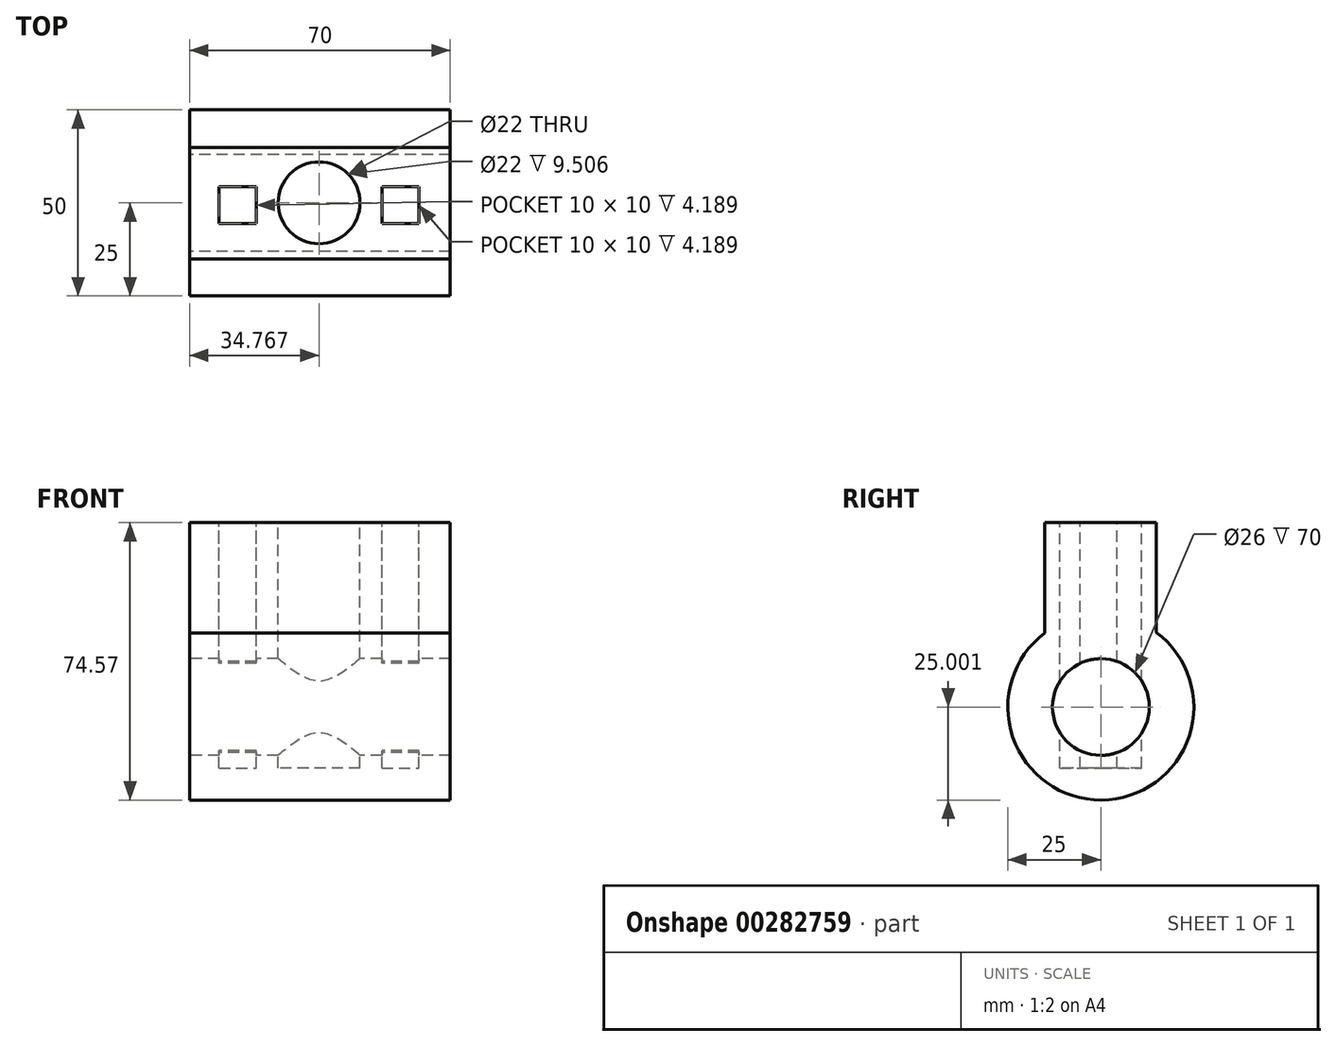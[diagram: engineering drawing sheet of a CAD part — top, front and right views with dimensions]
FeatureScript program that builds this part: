
annotation { "Feature Type Name" : "Feature", "Feature Type Description" : "" }
export const myFeature = defineFeature(function(context is Context, id is Id, definition is map)
    precondition{}
    {
        {
            var Q0;
            Q0=qCreatedBy(makeId("Top.planeOp"),FACE);
            var sketch = newSketch(context, id + "F0", { "sketchPlane" : qUnion([Q0])});
            skLineSegment(sketch, "E0.bottom", {"start": v(-48.83, 13.42) * mm, "end": v(21.17, 13.42) * mm});
            skLineSegment(sketch, "E0.top", {"start": v(-48.83, -16.58) * mm, "end": v(21.17, -16.58) * mm});
            skLineSegment(sketch, "E0.left", {"start": v(-48.83, 13.42) * mm, "end": v(-48.83, -16.58) * mm});
            skLineSegment(sketch, "E0.right", {"start": v(21.17, 13.42) * mm, "end": v(21.17, -16.58) * mm});
            skSolve(sketch);
        }
        {
            var Q0;
            Q0=makeQuery(id+"F0.imprint","IMPRINT",FACE,{"disambiguationData":[TD([[makeQuery(id+"F0.imprint","IMPRINT",EDGE,{"derivedFrom":sQuery(id+"F0.wireOp",EDGE,"E0.bottom")}),-1.0]])]});
            extrude(context, id + "F1", {"entities" : qUnion([Q0]), "depth" : 66 * mm});
        }
        {
            var Q0;
            Q0=makeQuery(id+"F1.opExtrude","CAP_FACE",FACE,{"disambiguationData":[OSD([sQuery(id+"F0.wireOp",EDGE,"E0.bottom"),sQuery(id+"F0.wireOp",EDGE,"E0.top"),sQuery(id+"F0.wireOp",EDGE,"E0.left"),sQuery(id+"F0.wireOp",EDGE,"E0.right")])],"isStart":false});
            var sketch = newSketch(context, id + "F2", { "sketchPlane" : qUnion([Q0])});
            skCircle(sketch, "E1", {"center": v(-14.06, -1.48) * mm, "radius": 11 * mm});
            skLineSegment(sketch, "E2.bottom", {"start": v(-40.94, 2.9) * mm, "end": v(-30.94, 2.9) * mm});
            skLineSegment(sketch, "E2.top", {"start": v(-40.94, -7.1) * mm, "end": v(-30.94, -7.1) * mm});
            skLineSegment(sketch, "E2.left", {"start": v(-40.94, 2.9) * mm, "end": v(-40.94, -7.1) * mm});
            skLineSegment(sketch, "E2.right", {"start": v(-30.94, 2.9) * mm, "end": v(-30.94, -7.1) * mm});
            skLineSegment(sketch, "E3.bottom", {"start": v(2.81, 2.9) * mm, "end": v(12.81, 2.9) * mm});
            skLineSegment(sketch, "E3.top", {"start": v(2.81, -7.1) * mm, "end": v(12.81, -7.1) * mm});
            skLineSegment(sketch, "E3.left", {"start": v(2.81, 2.9) * mm, "end": v(2.81, -7.1) * mm});
            skLineSegment(sketch, "E3.right", {"start": v(12.81, 2.9) * mm, "end": v(12.81, -7.1) * mm});
            skSolve(sketch);
        }
        {
            var Q0;
            Q0=makeQuery(id+"F2.imprint","IMPRINT",FACE,{"disambiguationData":[TD([[makeQuery(id+"F2.imprint","IMPRINT",EDGE,{"derivedFrom":sQuery(id+"F2.wireOp",EDGE,"E2.bottom")}),-1.0]])]});
            var Q1;
            Q1=makeQuery(id+"F2.imprint","IMPRINT",FACE,{"disambiguationData":[TD([[makeQuery(id+"F2.imprint","IMPRINT",EDGE,{"derivedFrom":sQuery(id+"F2.wireOp",EDGE,"E3.bottom")}),-1.0]])]});
            var Q2;
            Q2=makeQuery(id+"F2.imprint","IMPRINT",FACE,{"disambiguationData":[TD([[makeQuery(id+"F2.imprint","IMPRINT",EDGE,{"derivedFrom":sQuery(id+"F2.wireOp",EDGE,"E1")}),1.0]])]});
            extrude(context, id + "F3", {"entities" : qUnion([Q0, Q1, Q2]), "operationType" : NewBodyOperationType.REMOVE, "oppositeDirection" : true, "depth" : 66 * mm});
        }
        {
            var Q0;
            Q0=makeQuery(id+"F1.opExtrude","SWEPT_FACE",FACE,{"disambiguationData":[OSD([sQuery(id+"F0.wireOp",EDGE,"E0.left")])]});
            var sketch = newSketch(context, id + "F4", { "sketchPlane" : qUnion([Q0])});
            skCircle(sketch, "E4", {"center": v(1.48, 16.43) * mm, "radius": 25 * mm});
            skSolve(sketch);
        }
        {
            var Q0;
            {var subQ1=sQuery(id+"F0.wireOp",EDGE,"E0.left");var subQ6=makeQuery(id+"F1.opExtrude","CAP_EDGE",EDGE,{"disambiguationData":[OSD([subQ1])],"isStart":true});Q0=makeQuery(id+"F4.imprint","IMPRINT",FACE,{"disambiguationData":[TD([[makeQuery(id+"F4.imprint","IMPRINT",EDGE,{"derivedFrom":subQ6}),-1.0]])]});}
            extrude(context, id + "F5", {"entities" : qUnion([Q0]), "operationType" : NewBodyOperationType.ADD, "oppositeDirection" : true, "depth" : 70 * mm});
        }
        {
            var Q0;
            {var subQ0=sQuery(id+"F0.wireOp",EDGE,"E0.left");Q0=makeQuery(id+"F5.boolean.opBoolean","MERGE",FACE,{"derivedFrom":[makeQuery(id+"F1.opExtrude","SWEPT_FACE",FACE,{"disambiguationData":[OSD([subQ0])]}),makeQuery(id+"F5.opExtrude","CAP_FACE",FACE,{"disambiguationData":[OSD([sQuery(id+"F0.wireOp",EDGE,"E0.bottom"),sQuery(id+"F0.wireOp",EDGE,"E0.top"),subQ0,sQuery(id+"F4.wireOp",EDGE,"E4")])],"isStart":true})]});}
            var sketch = newSketch(context, id + "F6", { "sketchPlane" : qUnion([Q0])});
            skCircle(sketch, "E5", {"center": v(1.48, 16.43) * mm, "radius": 13 * mm});
            skSolve(sketch);
        }
        {
            var Q0;
            Q0=makeQuery(id+"F6.imprint","IMPRINT",FACE,{"disambiguationData":[TD([[makeQuery(id+"F6.imprint","IMPRINT",EDGE,{"derivedFrom":sQuery(id+"F6.wireOp",EDGE,"E5")}),1.0]])]});
            extrude(context, id + "F7", {"entities" : qUnion([Q0]), "operationType" : NewBodyOperationType.REMOVE, "oppositeDirection" : true, "depth" : 70 * mm});
        }
    });
